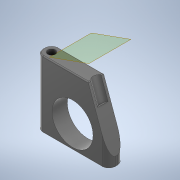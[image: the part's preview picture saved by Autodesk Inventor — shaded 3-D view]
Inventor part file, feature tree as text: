
AUTODESK INVENTOR PART (.ipt)
format: ipt  version: 2020 (Build 240168000, 168)  size: 227,840 bytes
history: native  units: mm
features: projected_geometry x9, extrude x6, sketch x5, other x2, fillet x2
ambient origin geometry x8: Origin, YZ Plane, XZ Plane, XY Plane, X Axis, Y Axis, Z Axis, Center Point
bodies: Body1 (feature_tree)
feature tree (24):
  other  "Твердое тело1"
  extrude  "Выдавливание1"  Depth=30.0mm
  fillet  "Сопряжение1"  Radius=4.0mm
  extrude  "Выдавливание2"  Depth=38.0mm
  extrude  "Выдавливание3"  Depth=8.0mm
  sketch  "Эскиз5"
  extrude  "Выдавливание4"  Depth=35.0mm TaperAngle=0.0deg
  extrude  "Выдавливание5"  Depth=3.5mm
  fillet  "Сопряжение2"  Radius=35.0mm
  other  "РабПлоскость1"
  extrude  "Выдавливание6"  Depth=35.0mm TaperAngle=0.0deg
  sketch  "Эскиз2"
  sketch  "Эскиз3"
  projected_geometry  "Спроецированная петля1"
  projected_geometry  "Спроецированная петля2"
  projected_geometry  "Спроецированная петля3"
  projected_geometry  "Спроецированная петля4"
  projected_geometry  "Спроецированная петля5"
  projected_geometry  "Спроецированная петля6"
  sketch  "Эскиз4"
  projected_geometry  "Спроецированная петля7"
  projected_geometry  "Спроецированная петля8"
  projected_geometry  "Спроецированная петля9"
  sketch  "Эскиз6"
